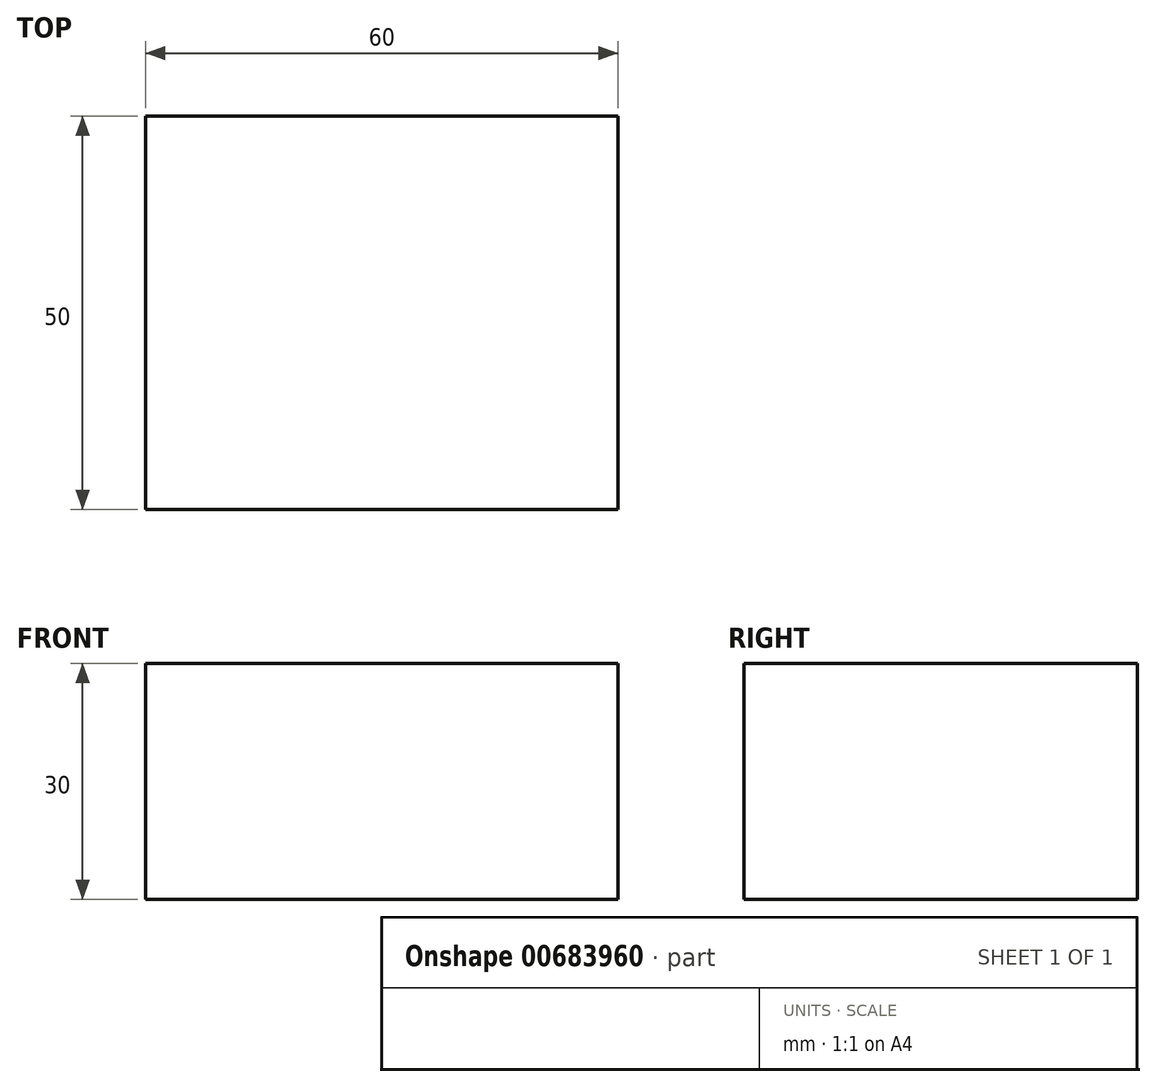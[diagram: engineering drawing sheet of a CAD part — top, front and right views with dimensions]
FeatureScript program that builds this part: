
annotation { "Feature Type Name" : "Feature", "Feature Type Description" : "" }
export const myFeature = defineFeature(function(context is Context, id is Id, definition is map)
    precondition{}
    {
        {
            var Q0;
            Q0=qCreatedBy(makeId("Front.planeOp"),FACE);
            var sketch = newSketch(context, id + "F0", { "sketchPlane" : qUnion([Q0])});
            skLineSegment(sketch, "E0.bottom", {"start": v(-43.18, -15.2) * mm, "end": v(16.82, -15.2) * mm});
            skLineSegment(sketch, "E0.top", {"start": v(-43.18, -45.2) * mm, "end": v(16.82, -45.2) * mm});
            skLineSegment(sketch, "E0.left", {"start": v(-43.18, -15.2) * mm, "end": v(-43.18, -45.2) * mm});
            skLineSegment(sketch, "E0.right", {"start": v(16.82, -15.2) * mm, "end": v(16.82, -45.2) * mm});
            skSolve(sketch);
        }
        {
            var Q0;
            Q0 = qSketchRegion(id + "F0", true);
            extrude(context, id + "F1", {"entities" : qUnion([Q0]), "depth" : 50 * mm, "offsetDistance" : 25.4 * mm});
        }
    });
